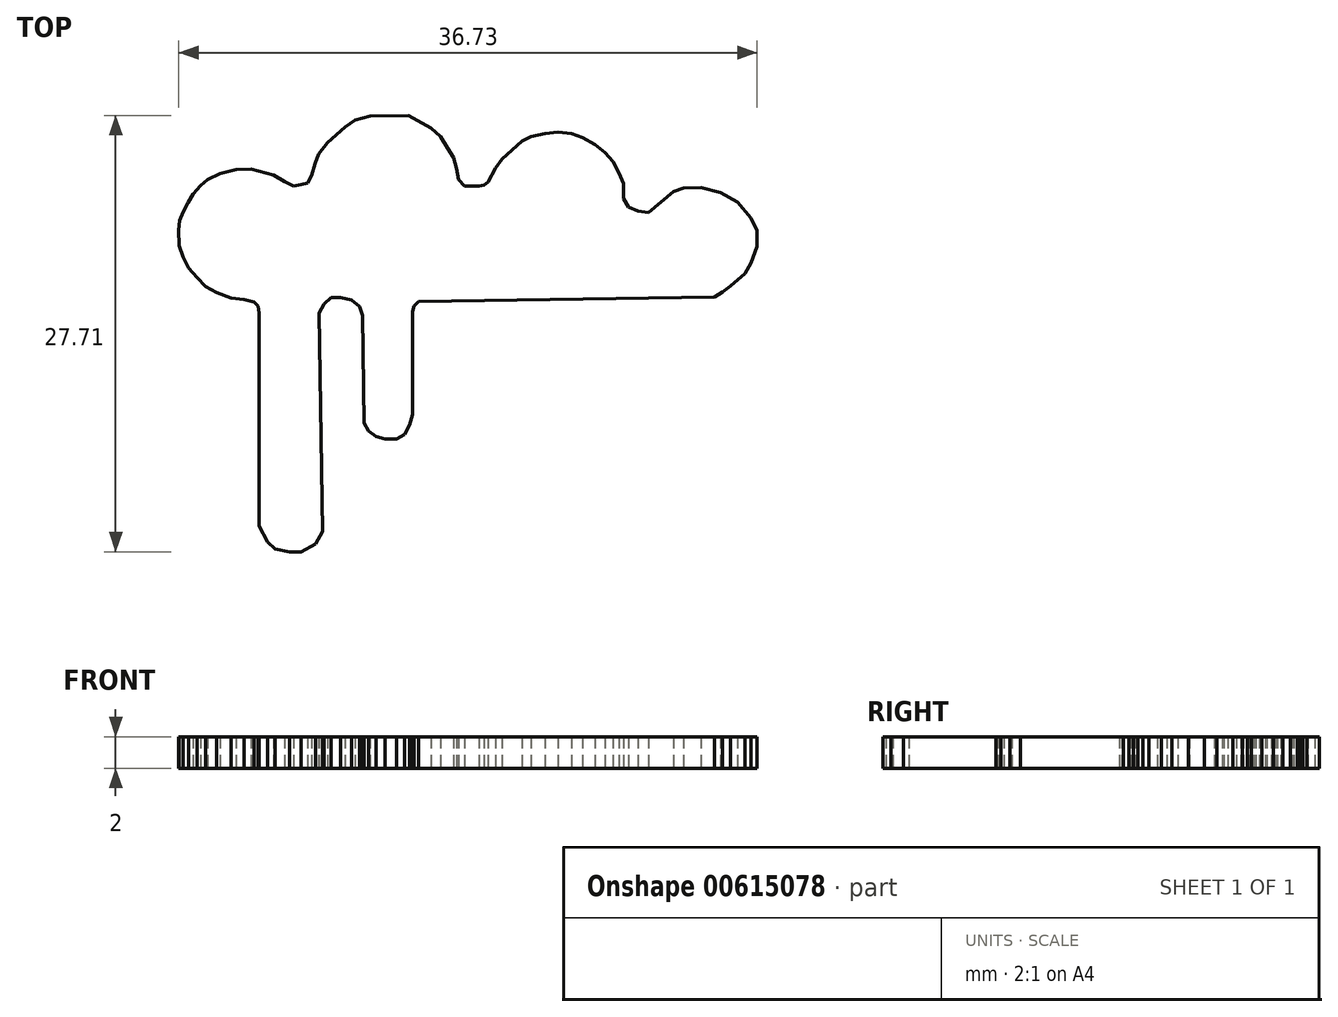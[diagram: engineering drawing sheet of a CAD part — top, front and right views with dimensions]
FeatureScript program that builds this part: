
annotation { "Feature Type Name" : "Feature", "Feature Type Description" : "" }
export const myFeature = defineFeature(function(context is Context, id is Id, definition is map)
    precondition{}
    {
        {
            var Q0;
            Q0=qCreatedBy(makeId("Top.planeOp"),FACE);
            var sketch = newSketch(context, id + "F0", { "sketchPlane" : qUnion([Q0])});
            skLineSegment(sketch, "E0", {"start": v(10.38, 45.8) * mm, "end": v(10.38, 32.24) * mm});
            skLineSegment(sketch, "E1", {"start": v(10.38, 32.24) * mm, "end": v(10.92, 31.24) * mm});
            skLineSegment(sketch, "E2", {"start": v(10.92, 31.24) * mm, "end": v(11.39, 30.78) * mm});
            skLineSegment(sketch, "E3", {"start": v(11.39, 30.78) * mm, "end": v(12.32, 30.6) * mm});
            skLineSegment(sketch, "E4", {"start": v(12.32, 30.6) * mm, "end": v(13.06, 30.6) * mm});
            skLineSegment(sketch, "E5", {"start": v(13.06, 30.6) * mm, "end": v(13.98, 31.12) * mm});
            skLineSegment(sketch, "E6", {"start": v(13.98, 31.12) * mm, "end": v(14.41, 31.9) * mm});
            skLineSegment(sketch, "E7", {"start": v(14.41, 31.9) * mm, "end": v(14.2, 45.77) * mm});
            skPoint(sketch, "E7.endSnap0", {"position": v(14.2, 31.52) * mm});
            skLineSegment(sketch, "E8", {"start": v(14.2, 45.77) * mm, "end": v(14.5, 46.34) * mm});
            skLineSegment(sketch, "E9", {"start": v(14.5, 46.34) * mm, "end": v(14.95, 46.75) * mm});
            skLineSegment(sketch, "E10", {"start": v(14.95, 46.75) * mm, "end": v(15.55, 46.76) * mm});
            skLineSegment(sketch, "E11", {"start": v(15.55, 46.76) * mm, "end": v(16.27, 46.62) * mm});
            skLineSegment(sketch, "E12", {"start": v(16.27, 46.62) * mm, "end": v(16.77, 46.2) * mm});
            skLineSegment(sketch, "E13", {"start": v(16.77, 46.2) * mm, "end": v(16.96, 45.63) * mm});
            skLineSegment(sketch, "E14", {"start": v(16.96, 45.63) * mm, "end": v(17.06, 38.8) * mm});
            skLineSegment(sketch, "E15", {"start": v(17.06, 38.8) * mm, "end": v(17.34, 38.3) * mm});
            skLineSegment(sketch, "E16", {"start": v(17.34, 38.3) * mm, "end": v(17.82, 37.93) * mm});
            skLineSegment(sketch, "E17", {"start": v(17.82, 37.93) * mm, "end": v(18.4, 37.78) * mm});
            skLineSegment(sketch, "E18", {"start": v(18.4, 37.78) * mm, "end": v(19.1, 37.79) * mm});
            skLineSegment(sketch, "E19", {"start": v(19.1, 37.79) * mm, "end": v(19.63, 38.08) * mm});
            skLineSegment(sketch, "E20", {"start": v(19.63, 38.08) * mm, "end": v(19.96, 38.67) * mm});
            skLineSegment(sketch, "E21", {"start": v(19.96, 38.67) * mm, "end": v(20.13, 39.34) * mm});
            skLineSegment(sketch, "E22", {"start": v(20.13, 39.34) * mm, "end": v(20.13, 45.87) * mm});
            skLineSegment(sketch, "E23", {"start": v(20.13, 45.87) * mm, "end": v(20.22, 46.24) * mm});
            skLineSegment(sketch, "E24", {"start": v(20.22, 46.24) * mm, "end": v(20.52, 46.5) * mm});
            skLineSegment(sketch, "E25", {"start": v(20.52, 46.5) * mm, "end": v(21.08, 46.51) * mm});
            skLineSegment(sketch, "E26", {"start": v(21.08, 46.51) * mm, "end": v(39.3, 46.8) * mm});
            skLineSegment(sketch, "E27", {"start": v(39.3, 46.8) * mm, "end": v(39.83, 47.12) * mm});
            skLineSegment(sketch, "E28", {"start": v(39.83, 47.12) * mm, "end": v(40.34, 47.48) * mm});
            skLineSegment(sketch, "E29", {"start": v(40.34, 47.48) * mm, "end": v(41.26, 48.27) * mm});
            skLineSegment(sketch, "E30", {"start": v(41.26, 48.27) * mm, "end": v(41.64, 48.96) * mm});
            skLineSegment(sketch, "E31", {"start": v(41.64, 48.96) * mm, "end": v(42.02, 50) * mm});
            skLineSegment(sketch, "E32", {"start": v(42.02, 50) * mm, "end": v(42, 51) * mm});
            skLineSegment(sketch, "E33", {"start": v(42, 51) * mm, "end": v(41.64, 51.82) * mm});
            skLineSegment(sketch, "E34", {"start": v(41.64, 51.82) * mm, "end": v(40.78, 52.82) * mm});
            skLineSegment(sketch, "E35", {"start": v(40.78, 52.82) * mm, "end": v(39.68, 53.42) * mm});
            skLineSegment(sketch, "E36", {"start": v(39.68, 53.42) * mm, "end": v(38.45, 53.74) * mm});
            skLineSegment(sketch, "E37", {"start": v(38.45, 53.74) * mm, "end": v(37.35, 53.72) * mm});
            skLineSegment(sketch, "E38", {"start": v(37.35, 53.72) * mm, "end": v(36.7, 53.5) * mm});
            skLineSegment(sketch, "E39", {"start": v(36.7, 53.5) * mm, "end": v(36, 52.9) * mm});
            skLineSegment(sketch, "E40", {"start": v(36, 52.9) * mm, "end": v(35.49, 52.46) * mm});
            skLineSegment(sketch, "E41", {"start": v(35.49, 52.46) * mm, "end": v(35.12, 52.15) * mm});
            skLineSegment(sketch, "E42", {"start": v(35.12, 52.15) * mm, "end": v(34.47, 52.24) * mm});
            skLineSegment(sketch, "E43", {"start": v(34.47, 52.24) * mm, "end": v(33.85, 52.5) * mm});
            skLineSegment(sketch, "E44", {"start": v(33.85, 52.5) * mm, "end": v(33.54, 53.06) * mm});
            skLineSegment(sketch, "E45", {"start": v(33.54, 53.06) * mm, "end": v(33.54, 54) * mm});
            skLineSegment(sketch, "E46", {"start": v(33.54, 54) * mm, "end": v(33.24, 54.68) * mm});
            skLineSegment(sketch, "E47", {"start": v(33.24, 54.68) * mm, "end": v(32.86, 55.4) * mm});
            skLineSegment(sketch, "E48", {"start": v(32.86, 55.4) * mm, "end": v(32.35, 55.99) * mm});
            skLineSegment(sketch, "E49", {"start": v(32.35, 55.99) * mm, "end": v(31.72, 56.48) * mm});
            skLineSegment(sketch, "E50", {"start": v(31.72, 56.48) * mm, "end": v(30.92, 56.91) * mm});
            skLineSegment(sketch, "E51", {"start": v(30.92, 56.91) * mm, "end": v(30.23, 57.16) * mm});
            skLineSegment(sketch, "E52", {"start": v(30.23, 57.16) * mm, "end": v(29.38, 57.26) * mm});
            skLineSegment(sketch, "E53", {"start": v(29.38, 57.26) * mm, "end": v(28.55, 57.16) * mm});
            skLineSegment(sketch, "E54", {"start": v(28.55, 57.16) * mm, "end": v(27.65, 57) * mm});
            skLineSegment(sketch, "E55", {"start": v(27.65, 57) * mm, "end": v(27.1, 56.69) * mm});
            skLineSegment(sketch, "E56", {"start": v(27.1, 56.69) * mm, "end": v(26.42, 56.1) * mm});
            skLineSegment(sketch, "E57", {"start": v(26.42, 56.1) * mm, "end": v(25.8, 55.57) * mm});
            skLineSegment(sketch, "E58", {"start": v(25.8, 55.57) * mm, "end": v(25.4, 55) * mm});
            skLineSegment(sketch, "E59", {"start": v(25.4, 55) * mm, "end": v(25.18, 54.6) * mm});
            skLineSegment(sketch, "E60", {"start": v(25.18, 54.6) * mm, "end": v(24.91, 54.11) * mm});
            skLineSegment(sketch, "E61", {"start": v(24.91, 54.11) * mm, "end": v(24.7, 53.92) * mm});
            skLineSegment(sketch, "E62", {"start": v(24.7, 53.92) * mm, "end": v(24.35, 53.86) * mm});
            skLineSegment(sketch, "E63", {"start": v(24.35, 53.86) * mm, "end": v(23.43, 53.84) * mm});
            skLineSegment(sketch, "E64", {"start": v(23.43, 53.84) * mm, "end": v(23.06, 54.27) * mm});
            skLineSegment(sketch, "E65", {"start": v(23.06, 54.27) * mm, "end": v(22.94, 54.96) * mm});
            skLineSegment(sketch, "E66", {"start": v(22.94, 54.96) * mm, "end": v(22.75, 55.64) * mm});
            skLineSegment(sketch, "E67", {"start": v(22.75, 55.64) * mm, "end": v(22.35, 56.27) * mm});
            skLineSegment(sketch, "E68", {"start": v(22.35, 56.27) * mm, "end": v(21.9, 57) * mm});
            skLineSegment(sketch, "E69", {"start": v(21.9, 57) * mm, "end": v(21.3, 57.54) * mm});
            skLineSegment(sketch, "E70", {"start": v(21.3, 57.54) * mm, "end": v(20.68, 57.88) * mm});
            skLineSegment(sketch, "E71", {"start": v(20.68, 57.88) * mm, "end": v(19.87, 58.32) * mm});
            skLineSegment(sketch, "E72", {"start": v(19.87, 58.32) * mm, "end": v(18.87, 58.3) * mm});
            skLineSegment(sketch, "E73", {"start": v(18.87, 58.3) * mm, "end": v(17.42, 58.28) * mm});
            skLineSegment(sketch, "E74", {"start": v(17.42, 58.28) * mm, "end": v(16.49, 58.03) * mm});
            skLineSegment(sketch, "E75", {"start": v(16.49, 58.03) * mm, "end": v(15.85, 57.58) * mm});
            skLineSegment(sketch, "E76", {"start": v(15.85, 57.58) * mm, "end": v(15.28, 57.08) * mm});
            skLineSegment(sketch, "E77", {"start": v(15.28, 57.08) * mm, "end": v(14.74, 56.61) * mm});
            skLineSegment(sketch, "E78", {"start": v(14.74, 56.61) * mm, "end": v(14.18, 55.88) * mm});
            skLineSegment(sketch, "E79", {"start": v(14.18, 55.88) * mm, "end": v(13.93, 55.26) * mm});
            skLineSegment(sketch, "E80", {"start": v(13.93, 55.26) * mm, "end": v(13.73, 54.5) * mm});
            skLineSegment(sketch, "E81", {"start": v(13.73, 54.5) * mm, "end": v(13.48, 54.05) * mm});
            skLineSegment(sketch, "E82", {"start": v(13.48, 54.05) * mm, "end": v(13.07, 53.94) * mm});
            skLineSegment(sketch, "E83", {"start": v(13.07, 53.94) * mm, "end": v(12.57, 53.85) * mm});
            skLineSegment(sketch, "E84", {"start": v(12.57, 53.85) * mm, "end": v(12.02, 54.13) * mm});
            skLineSegment(sketch, "E85", {"start": v(12.02, 54.13) * mm, "end": v(11.32, 54.55) * mm});
            skLineSegment(sketch, "E86", {"start": v(11.32, 54.55) * mm, "end": v(9.89, 54.91) * mm});
            skLineSegment(sketch, "E87", {"start": v(9.89, 54.91) * mm, "end": v(8.92, 54.9) * mm});
            skLineSegment(sketch, "E88", {"start": v(8.92, 54.9) * mm, "end": v(7.9, 54.63) * mm});
            skLineSegment(sketch, "E89", {"start": v(7.9, 54.63) * mm, "end": v(7.13, 54.27) * mm});
            skLineSegment(sketch, "E90", {"start": v(7.13, 54.27) * mm, "end": v(6.66, 53.87) * mm});
            skLineSegment(sketch, "E91", {"start": v(6.66, 53.87) * mm, "end": v(6.19, 53.34) * mm});
            skLineSegment(sketch, "E92", {"start": v(6.19, 53.34) * mm, "end": v(5.87, 52.8) * mm});
            skLineSegment(sketch, "E93", {"start": v(5.87, 52.8) * mm, "end": v(5.55, 52.2) * mm});
            skLineSegment(sketch, "E94", {"start": v(5.55, 52.2) * mm, "end": v(5.35, 51.64) * mm});
            skLineSegment(sketch, "E95", {"start": v(5.35, 51.64) * mm, "end": v(5.29, 51.03) * mm});
            skLineSegment(sketch, "E96", {"start": v(5.29, 51.03) * mm, "end": v(5.3, 50.06) * mm});
            skLineSegment(sketch, "E97", {"start": v(5.3, 50.06) * mm, "end": v(5.56, 49.33) * mm});
            skLineSegment(sketch, "E98", {"start": v(5.56, 49.33) * mm, "end": v(5.92, 48.64) * mm});
            skLineSegment(sketch, "E99", {"start": v(5.92, 48.64) * mm, "end": v(6.43, 48.04) * mm});
            skLineSegment(sketch, "E100", {"start": v(6.43, 48.04) * mm, "end": v(6.99, 47.48) * mm});
            skLineSegment(sketch, "E101", {"start": v(6.99, 47.48) * mm, "end": v(7.68, 47.08) * mm});
            skLineSegment(sketch, "E102", {"start": v(7.68, 47.08) * mm, "end": v(8.6, 46.73) * mm});
            skLineSegment(sketch, "E103", {"start": v(8.6, 46.73) * mm, "end": v(9.45, 46.65) * mm});
            skLineSegment(sketch, "E104", {"start": v(9.45, 46.65) * mm, "end": v(10.08, 46.48) * mm});
            skLineSegment(sketch, "E105", {"start": v(10.08, 46.48) * mm, "end": v(10.32, 46.21) * mm});
            skLineSegment(sketch, "E106", {"start": v(10.32, 46.21) * mm, "end": v(10.38, 45.8) * mm});
            skSolve(sketch);
        }
        {
            var Q0;
            Q0 = qSketchRegion(id + "F0", true);
            extrude(context, id + "F1", {"entities" : qUnion([Q0]), "depth" : 2 * mm, "offsetDistance" : 25 * mm});
        }
    });
